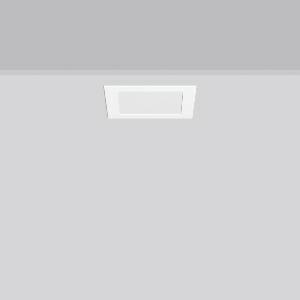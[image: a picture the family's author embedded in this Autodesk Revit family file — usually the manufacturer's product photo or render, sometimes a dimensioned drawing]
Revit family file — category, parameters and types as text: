
# Revit family: toledo_flat_square_e_901486_002_1_76_a8fa
name_source: partatom
category: Lighting Fixtures
units: mm (PartAtom-declared; Revit-internal decimal feet)

## family parameters
Cut with Voids When Loaded = No
Host = Face
Light Source = No
Part Type = Normal
Room Calculation Point = No
Round Connector Dimension = Use Diameter
Shared = No

## types (1)
- TOLEDO FLAT square E (1 x LED Modul 840, 800 lm, 4000)
    Apparent Load = 8 VA
    CIE Flux Codes = 49 80 96 100 100
    Color Rendering = 80
    Color Temperature = 4000
    Default Elevation = 1800 mm
    Description = Series: TOLEDO FLAT square
Ultra thin recessed downlight. Housing: die-cast aluminium. Light guide and diffuser made of non-yellowing PMMA, opal matt. Ceiling installation with spring system. Mounting depth depends on ceiling strength. Suitable for through-wiring with separately available accessories. Surface mounted housing as accessory for all sizes. Retrofittable decorative cylinders made of chintz fabric as accessory, optional with satin finish plastic diffuser. Through-wiring box (5 pole) available as accessory. 
Colour: white
Length: 172 mm
Width: 172 mm
Height: 3 mm
Cut-out length: 156 mm
Cut-out width: 156 mm
Recess height: 31-56 mm
Luminaire: recess height: 31-51 mm
Lamp: LED
Socket: without socket
Colour temperature: 4000K
Colour rendering index (CRI): 80
System power: 8 W
Rated luminous flux: 800 lm
Luminous efficiency: 100 lm/W
Control gear: Converter, dimmable, DALI
Protection class: II
Type of protection: IP 54
    Height = 0 mm  [stored 0 ft]
    Lamp = 1 x LED Modul 840
    Lamp Light Flux = 800 lm
    Lamp count = 1
    Length = 172 mm
    Lifetime = 50000 h
    Luminous efficacy = 100 lm/W
    Manufacturer = RZB
    ModVariant = No
    Model = 901486.002.1.76
    Mounting Place = Ceiling
    Mounting Type = Recessed
    Number of Poles = 1
    OnlyDefault = Yes
    Power Factor = 1
    Product Name = TOLEDO FLAT square E
    Product group = Recessed downlights
    ProductGroupID = 402
    Protection Class = Protection class II
    Protection Degree = IP 20
    RLX_Detail_Level = 1
    RLX_Emergency_Light_Flux = 0 lm
    RLX_Emergency_Type = 0
    RLX_Emergency_Type_DB = No
    RlxData = <blob elided: 57685 chars, md5=223fcfa9>
    Socket = socket
    Standby Power = 0 W
    System Light Flux = 800 lm
    System Power = 8 W
    Type Comments = Product without accessories
    Type Image = 901486.002.jpg
    URL = http://relux.com
    VarID = ---
    Voltage = 230 V
    Voltage Range = 220-240 V
    Weight = 0.00 kg
    Width = 172 mm

note: [stored X ft] marks values corroborated as IEEE doubles in the binary element streams (Revit-internal decimal feet)

## geometry (parser evidence)
native form markers: Blend x4, Sweep x9
no freeform markers — native parametric forms only
